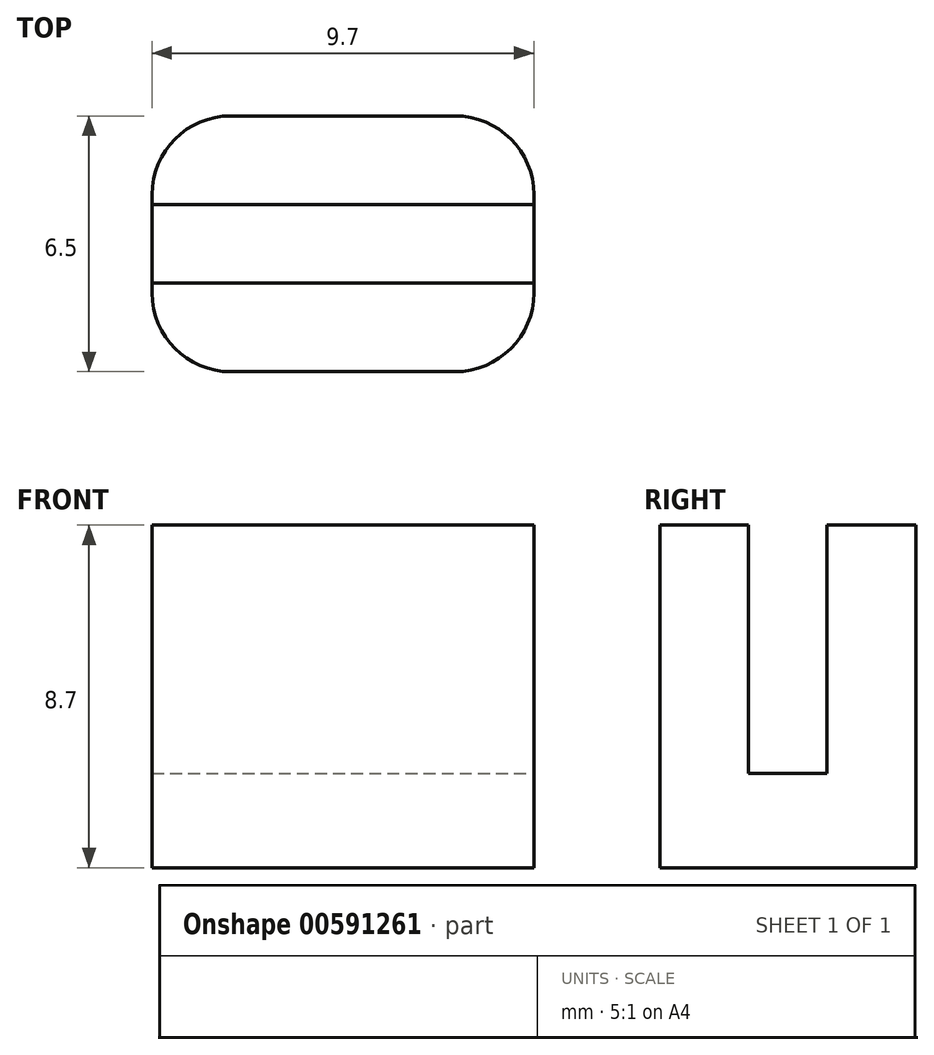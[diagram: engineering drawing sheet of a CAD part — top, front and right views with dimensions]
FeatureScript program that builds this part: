
annotation { "Feature Type Name" : "Feature", "Feature Type Description" : "" }
export const myFeature = defineFeature(function(context is Context, id is Id, definition is map)
    precondition{}
    {
        {
            var Q0;
            Q0=qCreatedBy(makeId("Top.planeOp"),FACE);
            var sketch = newSketch(context, id + "F0", { "sketchPlane" : qUnion([Q0])});
            skLineSegment(sketch, "E0.bottom", {"start": v(-4.85, 3.25) * mm, "end": v(4.85, 3.25) * mm});
            skLineSegment(sketch, "E0.top", {"start": v(-4.85, -3.25) * mm, "end": v(4.85, -3.25) * mm});
            skLineSegment(sketch, "E0.left", {"start": v(-4.85, 3.25) * mm, "end": v(-4.85, -3.25) * mm});
            skLineSegment(sketch, "E0.right", {"start": v(4.85, 3.25) * mm, "end": v(4.85, -3.25) * mm});
            skSolve(sketch);
        }
        {
            var Q0;
            Q0 = qSketchRegion(id + "F0", true);
            extrude(context, id + "F1", {"entities" : qUnion([Q0]), "depth" : 8.7 * mm, "offsetDistance" : 25 * mm});
        }
        {
            var Q0;
            Q0=makeQuery(id+"F1.opExtrude","CAP_FACE",FACE,{"disambiguationData":[OSD([sQuery(id+"F0.wireOp",EDGE,"E0.bottom"),sQuery(id+"F0.wireOp",EDGE,"E0.top"),sQuery(id+"F0.wireOp",EDGE,"E0.left"),sQuery(id+"F0.wireOp",EDGE,"E0.right")])],"isStart":false});
            var sketch = newSketch(context, id + "F2", { "sketchPlane" : qUnion([Q0])});
            skLineSegment(sketch, "E1.bottom", {"start": v(-4.85, 1) * mm, "end": v(4.85, 1) * mm});
            skLineSegment(sketch, "E1.top", {"start": v(-4.85, -1) * mm, "end": v(4.85, -1) * mm});
            skLineSegment(sketch, "E1.left", {"start": v(-4.85, 1) * mm, "end": v(-4.85, -1) * mm});
            skLineSegment(sketch, "E1.right", {"start": v(4.85, 1) * mm, "end": v(4.85, -1) * mm});
            skSolve(sketch);
        }
        {
            var Q0;
            Q0 = qSketchRegion(id + "F2", true);
            extrude(context, id + "F3", {"entities" : qUnion([Q0]), "operationType" : NewBodyOperationType.REMOVE, "oppositeDirection" : true, "depth" : 6.3 * mm, "offsetDistance" : 25 * mm});
        }
        {
            var Q0;
            Q0=makeQuery(id+"F1.opExtrude","SWEPT_EDGE",EDGE,{"disambiguationData":[OSD([sQuery(id+"F0.wireOp",EDGE,"E0.bottom"),sQuery(id+"F0.wireOp",EDGE,"E0.left")])]});
            var Q1;
            Q1=makeQuery(id+"F1.opExtrude","SWEPT_EDGE",EDGE,{"disambiguationData":[OSD([sQuery(id+"F0.wireOp",EDGE,"E0.top"),sQuery(id+"F0.wireOp",EDGE,"E0.left")])]});
            var Q2;
            Q2=makeQuery(id+"F1.opExtrude","SWEPT_EDGE",EDGE,{"disambiguationData":[OSD([sQuery(id+"F0.wireOp",EDGE,"E0.top"),sQuery(id+"F0.wireOp",EDGE,"E0.right")])]});
            var Q3;
            Q3=makeQuery(id+"F1.opExtrude","SWEPT_EDGE",EDGE,{"disambiguationData":[OSD([sQuery(id+"F0.wireOp",EDGE,"E0.bottom"),sQuery(id+"F0.wireOp",EDGE,"E0.right")])]});
            fillet(context, id + "F4", {"entities" : qUnion([Q0, Q1, Q2, Q3]), "radius" : 2 * mm, "tangentPropagation" : true, "allowEdgeOverflow" : false});
        }
    });
